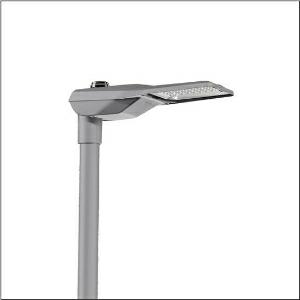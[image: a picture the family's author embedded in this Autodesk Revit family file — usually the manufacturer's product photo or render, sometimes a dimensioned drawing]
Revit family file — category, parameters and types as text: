
# Revit family: streetlight_sl_21_mini___stw1_0a_5xe6e47n08hb_d0ec
name_source: partatom
category: Lighting Fixtures
units: mm (PartAtom-declared; Revit-internal decimal feet)

## family parameters
Cut with Voids When Loaded = No
Host = Face
Light Source = No
Part Type = Normal
Room Calculation Point = No
Round Connector Dimension = Use Diameter
Shared = No

## types (1)
- --- (1 x LED, 9430 lm, 66 W, 4000K)
    Apparent Load = 66 VA
    CIE Flux Codes = 38 75 98 100 100
    Color Rendering = 70
    Color Temperature = 4000K
    Default Elevation = 1800 mm
    Description = Streetlight SL 21 mini, mast luminaire, primary light control with lens, of PMMA, primary optical cover: cover, of toughened safety glass, transparent, light distribution: STW1.0a, light emission: direct distribution, primary light characteristic: asymmetric, installation type: side-entry, LED, 3G 1.5mm², High Power LED, rated luminous flux: 9.430lm, luminous efficacy: 143lm/W, light colour: 740, colour temperature: 4000K, control gear: NEMA (7pin), control: overheat protection, pre-setting: linear dimming characteristic, constant luminous flux control, time-dependent luminous flux control, flexible luminous flux parameterisation, mains connection: 230..240V, AC, 50/60Hz, connection cable pre-assembled, cable length: 8,5m, wiring characteristics: H07RN-F, start of lifetime: 66W, end of service life: 69W, reduction: 30W, luminaire housing, of diecast aluminium (EN AC-44300), powder-coated, Siteco® metallic grey (DB 702S), corrosivity category C5 mid according to DIN EN ISO 12944, multi-level sealing system, sealing non-destructively replaceable, inclination adjustable: 0°, 5°, 10°, 15°, length: 628mm, width: 235mm, height: 110mm, spigot size: 42mm (side-entry), mounting height: 4..8m, protection rating (complete): IP66, insulation class (complete): insulation class I (protective earthing), certification: CE, ENEC, ENEC+, VDE, impact resistance: IK10, permissible operating ambient temperature for outdoor applications: -40..+50°C, standard-compliant lighting for roads and squares, packaging unit: 1 piece

Light Distribution: STW1.0a
    Height = 110 mm
    Lamp = 1 x LED
    Lamp Light Flux = 9430 lm
    Lamp Power = 66 W
    Lamp count = 1
    Length = 625 mm
    Luminous efficacy = 143 lm/W
    Manufacturer = Siteco
    ModVariant = No
    Model = 5XE6E47N08HB
    Number of Poles = 1
    OnlyDefault = Yes
    Power Factor = 1
    Product Name = Streetlight SL 21 mini | STW1.0a
    Product group = mast luminaire | pylon top
    ProductGroupID = 6100
    Protection Class = Protection class I
    Protection Degree = IP 66
    RLX_Detail_Level = 1
    RLX_Emergency_Light_Flux = 0 lm
    RLX_Emergency_Type = 0
    RLX_Emergency_Type_DB = No
    RlxData = <blob elided: 26189 chars, md5=f0460ae5>
    Socket = socket
    Standby Power = 0 W
    System Light Flux = 9430 lm
    System Power = 66 W
    Type Comments = factory setting: luminous flux: 100 % | dim-lin: 254 | 670 mA
    Type Image = l_1294379.jpg
    URL = http://relux.com
    VarID = @adj_157077
    Voltage = 0 V
    Weight = 0.00 kg
    Width = 234 mm

## geometry (parser evidence)
native form markers: Blend x4, Sweep x12
no freeform markers — native parametric forms only
